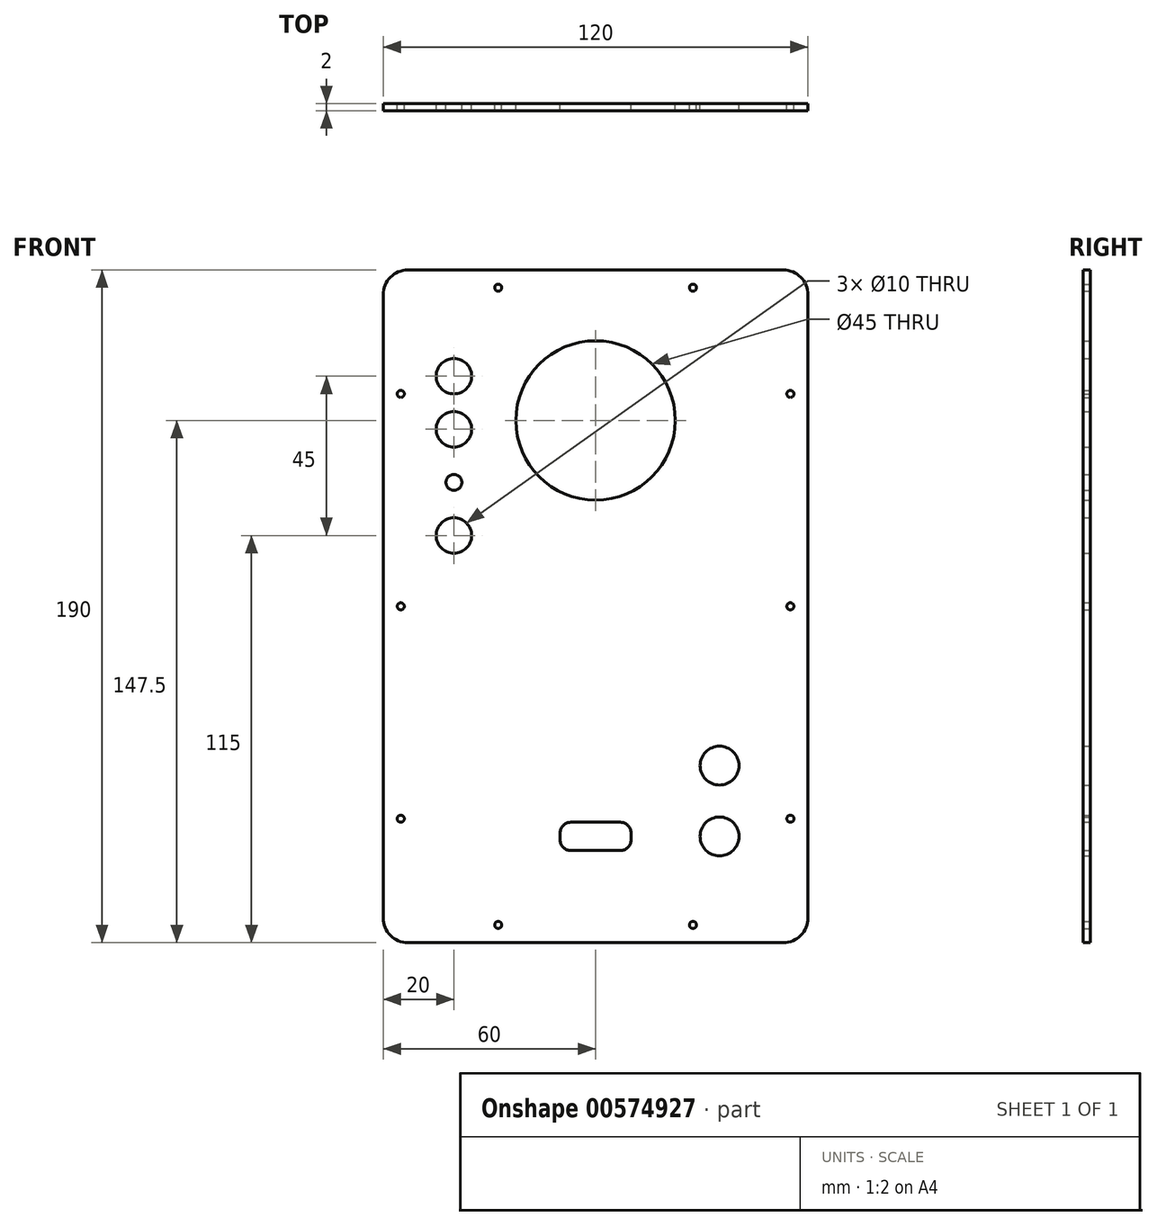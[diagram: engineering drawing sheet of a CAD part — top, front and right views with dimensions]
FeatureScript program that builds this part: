
annotation { "Feature Type Name" : "Feature", "Feature Type Description" : "" }
export const myFeature = defineFeature(function(context is Context, id is Id, definition is map)
    precondition{}
    {
        {
            var Q0;
            Q0=qCreatedBy(makeId("Front.planeOp"),FACE);
            var sketch = newSketch(context, id + "F0", { "sketchPlane" : qUnion([Q0])});
            skLineSegment(sketch, "E0.bottom", {"start": v(53, 95) * mm, "end": v(-53, 95) * mm});
            skLineSegment(sketch, "E0.top", {"start": v(53, -95) * mm, "end": v(-53, -95) * mm});
            skLineSegment(sketch, "E0.left", {"start": v(60, 88) * mm, "end": v(60, -88) * mm});
            skLineSegment(sketch, "E0.right", {"start": v(-60, 88) * mm, "end": v(-60, -88) * mm});
            skPoint(sketch, "E0.middle", {"position": v(0, 0) * mm});
            skPoint(sketch, "E1.visualSharp", {"position": v(-60, 95) * mm});
            skArc(sketch, "E1.filletArc", {"start": v(-53, 95) * mm, "mid": v(-57.95, 92.95) * mm, "end": v(-60, 88) * mm});
            skPoint(sketch, "E2.visualSharp", {"position": v(60, 95) * mm});
            skArc(sketch, "E2.filletArc", {"start": v(60, 88) * mm, "mid": v(57.95, 92.95) * mm, "end": v(53, 95) * mm});
            skPoint(sketch, "E3.visualSharp", {"position": v(60, -95) * mm});
            skArc(sketch, "E3.filletArc", {"start": v(53, -95) * mm, "mid": v(57.95, -92.95) * mm, "end": v(60, -88) * mm});
            skPoint(sketch, "E4.visualSharp", {"position": v(-60, -95) * mm});
            skArc(sketch, "E4.filletArc", {"start": v(-60, -88) * mm, "mid": v(-57.95, -92.95) * mm, "end": v(-53, -95) * mm});
            skPoint(sketch, "E5", {"position": v(-27.5, 90) * mm});
            skPoint(sketch, "E6", {"position": v(27.5, 90) * mm});
            skPoint(sketch, "E7", {"position": v(-55, -60) * mm});
            skPoint(sketch, "E8", {"position": v(-55, 60) * mm});
            skPoint(sketch, "E9", {"position": v(-55, 0) * mm});
            skPoint(sketch, "E10.MirrorP", {"position": v(55, 60) * mm});
            skPoint(sketch, "E11.MirrorP", {"position": v(55, 0) * mm});
            skPoint(sketch, "E12.MirrorP", {"position": v(55, -60) * mm});
            skPoint(sketch, "E13.MirrorP", {"position": v(-27.5, -90) * mm});
            skPoint(sketch, "E14.MirrorP", {"position": v(27.5, -90) * mm});
            skCircle(sketch, "E15", {"center": v(35, -65) * mm, "radius": 5.5 * mm});
            skCircle(sketch, "E16", {"center": v(35, -45) * mm, "radius": 5.5 * mm});
            skLineSegment(sketch, "E17", {"start": v(0, 0) * mm, "end": v(0, -64.73) * mm, "construction": true});
            skCircle(sketch, "E18", {"center": v(0, 52.5) * mm, "radius": 22.5 * mm});
            skCircle(sketch, "E19", {"center": v(-40, 65) * mm, "radius": 5 * mm});
            skCircle(sketch, "E20", {"center": v(-40, 50) * mm, "radius": 5 * mm});
            skCircle(sketch, "E21", {"center": v(-40, 35) * mm, "radius": 2.25 * mm});
            skCircle(sketch, "E22", {"center": v(-40, 20) * mm, "radius": 5 * mm});
            skLineSegment(sketch, "E23.bottom", {"start": v(7, -69) * mm, "end": v(-7, -69) * mm});
            skLineSegment(sketch, "E23.top", {"start": v(7, -61) * mm, "end": v(-7, -61) * mm});
            skLineSegment(sketch, "E23.left", {"start": v(10, -66) * mm, "end": v(10, -64) * mm});
            skLineSegment(sketch, "E23.right", {"start": v(-10, -66) * mm, "end": v(-10, -64) * mm});
            skPoint(sketch, "E23.middle", {"position": v(0, -65) * mm});
            skPoint(sketch, "E24.visualSharp", {"position": v(-10, -61) * mm});
            skArc(sketch, "E24.filletArc", {"start": v(-7, -61) * mm, "mid": v(-9.12, -61.88) * mm, "end": v(-10, -64) * mm});
            skPoint(sketch, "E25.visualSharp", {"position": v(-10, -69) * mm});
            skArc(sketch, "E25.filletArc", {"start": v(-10, -66) * mm, "mid": v(-9.12, -68.12) * mm, "end": v(-7, -69) * mm});
            skPoint(sketch, "E26.visualSharp", {"position": v(10, -69) * mm});
            skArc(sketch, "E26.filletArc", {"start": v(7, -69) * mm, "mid": v(9.12, -68.12) * mm, "end": v(10, -66) * mm});
            skPoint(sketch, "E27.visualSharp", {"position": v(10, -61) * mm});
            skArc(sketch, "E27.filletArc", {"start": v(10, -64) * mm, "mid": v(9.12, -61.88) * mm, "end": v(7, -61) * mm});
            skSolve(sketch);
        }
        {
            var Q0;
            Q0=makeQuery(id+"F0.imprint","IMPRINT",FACE,{"disambiguationData":[TD([[makeQuery(id+"F0.imprint","IMPRINT",EDGE,{"derivedFrom":sQuery(id+"F0.wireOp",EDGE,"E0.bottom")}),1.0]])]});
            extrude(context, id + "F1", {"entities" : qUnion([Q0]), "depth" : 2 * mm, "offsetDistance" : 25 * mm});
        }
        {
            var Q0;
            Q0=sQuery(id+"F0.wireOp",VERTEX,"E5");
            var Q1;
            Q1=sQuery(id+"F0.wireOp",VERTEX,"E8");
            var Q2;
            Q2=sQuery(id+"F0.wireOp",VERTEX,"E9");
            var Q3;
            Q3=sQuery(id+"F0.wireOp",VERTEX,"E7");
            var Q4;
            Q4=sQuery(id+"F0.wireOp",VERTEX,"E13.MirrorP");
            var Q5;
            Q5=sQuery(id+"F0.wireOp",VERTEX,"E14.MirrorP");
            var Q6;
            Q6=sQuery(id+"F0.wireOp",VERTEX,"E12.MirrorP");
            var Q7;
            Q7=sQuery(id+"F0.wireOp",VERTEX,"E11.MirrorP");
            var Q8;
            Q8=sQuery(id+"F0.wireOp",VERTEX,"E10.MirrorP");
            var Q9;
            Q9=sQuery(id+"F0.wireOp",VERTEX,"E6");
            var Q10;
            Q10=makeQuery(id+"F1.opExtrude","SWEPT_BODY",BODY,{"disambiguationData":[OSD([sQuery(id+"F0.wireOp",EDGE,"E0.bottom"),sQuery(id+"F0.wireOp",EDGE,"E0.top"),sQuery(id+"F0.wireOp",EDGE,"E0.left"),sQuery(id+"F0.wireOp",EDGE,"E0.right"),sQuery(id+"F0.wireOp",EDGE,"E1.filletArc"),sQuery(id+"F0.wireOp",EDGE,"E2.filletArc"),sQuery(id+"F0.wireOp",EDGE,"E3.filletArc"),sQuery(id+"F0.wireOp",EDGE,"E4.filletArc")])]});
            hole(context, id + "F2", {"style" : HoleStyle.SIMPLE, "endStyle" : HoleEndStyle.THROUGH, "oppositeDirection" : true, "holeDiameter" : 2 * mm, "isTappedThrough" : true, "tappedDepth" : 12 * mm, "tapClearance" : 3, "locations" : qUnion([Q0, Q1, Q2, Q3, Q4, Q5, Q6, Q7, Q8, Q9]), "scope" : qUnion([Q10]), "majorDiameter" : 5 * mm});
        }
    });
